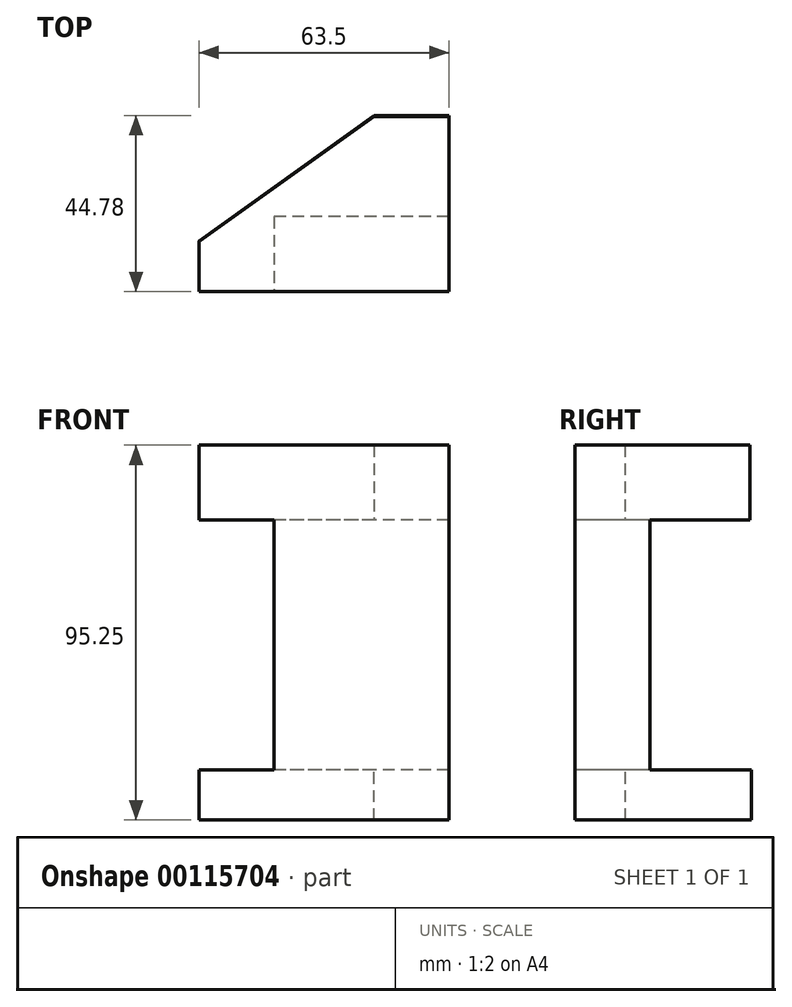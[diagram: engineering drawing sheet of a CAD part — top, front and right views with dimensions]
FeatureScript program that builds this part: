
annotation { "Feature Type Name" : "Feature", "Feature Type Description" : "" }
export const myFeature = defineFeature(function(context is Context, id is Id, definition is map)
    precondition{}
    {
        {
            var Q0;
            Q0=qCreatedBy(makeId("Top.planeOp"),FACE);
            var sketch = newSketch(context, id + "F0", { "sketchPlane" : qUnion([Q0])});
            skLineSegment(sketch, "E0", {"start": v(0, 0) * mm, "end": v(63.5, 0) * mm});
            skLineSegment(sketch, "E1", {"start": v(63.5, 0) * mm, "end": v(63.5, 44.45) * mm});
            skLineSegment(sketch, "E2", {"start": v(63.5, 44.45) * mm, "end": v(44.45, 44.45) * mm});
            skLineSegment(sketch, "E3", {"start": v(44.45, 44.45) * mm, "end": v(0, 12.7) * mm});
            skLineSegment(sketch, "E4", {"start": v(0, 12.7) * mm, "end": v(0, 0) * mm});
            skSolve(sketch);
        }
        {
            var Q0;
            Q0 = qSketchRegion(id + "F0", true);
            var Q1;
            Q1=makeQuery(id+"F0.imprint","IMPRINT",FACE,{"disambiguationData":[TD([[makeQuery(id+"F0.imprint","IMPRINT",EDGE,{"derivedFrom":sQuery(id+"F0.wireOp",EDGE,"E0")}),1.0]])]});
            extrude(context, id + "F1", {"entities" : qUnion([Q0, Q1]), "depth" : 19.05 * mm});
        }
        {
            var Q0;
            Q0=qCreatedBy(makeId("Front.planeOp"),FACE);
            var sketch = newSketch(context, id + "F2", { "sketchPlane" : qUnion([Q0])});
            skLineSegment(sketch, "E5.bottom", {"start": v(63.5, 0) * mm, "end": v(19.05, 0) * mm});
            skLineSegment(sketch, "E5.top", {"start": v(63.5, -63.5) * mm, "end": v(19.05, -63.5) * mm});
            skLineSegment(sketch, "E5.left", {"start": v(63.5, 0) * mm, "end": v(63.5, -63.5) * mm});
            skLineSegment(sketch, "E5.right", {"start": v(19.05, 0) * mm, "end": v(19.05, -63.5) * mm});
            skLineSegment(sketch, "E6", {"start": v(63.5, -31.75) * mm, "end": v(19.05, -31.75) * mm, "construction": true});
            skSolve(sketch);
        }
        {
            var Q0;
            Q0=makeQuery(id+"F2.imprint","IMPRINT",FACE,{"disambiguationData":[TD([[makeQuery(id+"F2.imprint","IMPRINT",EDGE,{"derivedFrom":sQuery(id+"F2.wireOp",EDGE,"E5.bottom")}),1.0]])]});
            extrude(context, id + "F3", {"entities" : qUnion([Q0]), "operationType" : NewBodyOperationType.ADD, "oppositeDirection" : true, "depth" : 19.05 * mm});
        }
        {
            var Q0;
            Q0=makeQuery(id+"F3.opExtrude","SWEPT_FACE",FACE,{"disambiguationData":[OSD([sQuery(id+"F2.wireOp",EDGE,"E5.top")])]});
            var sketch = newSketch(context, id + "F4", { "sketchPlane" : qUnion([Q0])});
            skLineSegment(sketch, "E7", {"start": v(0, 0) * mm, "end": v(63.5, 0) * mm});
            skLineSegment(sketch, "E8", {"start": v(63.5, 0) * mm, "end": v(63.5, -44.78) * mm});
            skLineSegment(sketch, "E9", {"start": v(63.5, -44.78) * mm, "end": v(44.51, -44.78) * mm});
            skLineSegment(sketch, "E10", {"start": v(44.51, -44.78) * mm, "end": v(0, -12.83) * mm});
            skLineSegment(sketch, "E11", {"start": v(0, -12.83) * mm, "end": v(0, 0) * mm});
            skSolve(sketch);
        }
        {
            var Q0;
            {var subQ0=sQuery(id+"F4.wireOp",EDGE,"E9");Q0=makeQuery(id+"F4.imprint","IMPRINT",FACE,{"disambiguationData":[TD([[makeQuery(id+"F4.imprint","IMPRINT",EDGE,{"derivedFrom":subQ0}),-1.0]])]});}
            var Q1;
            {var subQ3=sQuery(id+"F2.wireOp",EDGE,"E5.top");var subQ5=makeQuery(id+"F3.opExtrude","CAP_EDGE",EDGE,{"disambiguationData":[OSD([subQ3])],"isStart":false});Q1=makeQuery(id+"F4.imprint","IMPRINT",FACE,{"disambiguationData":[TD([[makeQuery(id+"F4.imprint","IMPRINT",EDGE,{"derivedFrom":subQ5}),-1.0]])]});}
            extrude(context, id + "F5", {"entities" : qUnion([Q0, Q1]), "operationType" : NewBodyOperationType.ADD, "depth" : 12.7 * mm});
        }
    });
